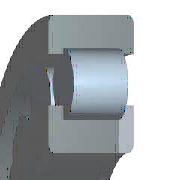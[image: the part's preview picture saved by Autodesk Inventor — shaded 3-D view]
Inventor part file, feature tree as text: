
AUTODESK INVENTOR PART (.ipt)
format: ipt  version: 2020 (Build 240168000, 168)  size: 294,912 bytes
history: native  units: mm (DEFAULTED — no unit token found)
features: sketch x1, pattern_circular x1, fillet x1
ambient origin geometry x8: Origin, YZ Plane, XZ Plane, XY Plane, X Axis, Y Axis, Z Axis, Center Point
bodies: Solid1 (feature_tree), BODY (feature_tree)
feature tree (3):
  sketch  "草图"  dims[d64=90.0deg d0=90.0mm d1=360.0deg d4=0.0mm d5=0.0mm d6=0.0mm d7=40.0mm d8=49.5mm d9=53.4mm d10=66.6mm d11=80.0mm d12=71.5mm d13=4.5mm d14=18.0mm d15=0.0mm d16=0.0mm d89=90.0deg d90=1.1mm d91=1.1mm]
  pattern_circular  "IDS_ARRAYROLLER[SIMPL:T]"  Count=9 Angle=360.0deg
  fillet  "Fillet1"  [1 undecoded]
note: 1 required parameter value undecoded (feature->parameter linkage not recoverable at this tier; creation-order binding heuristic only, values carry confidence <= 0.55)
